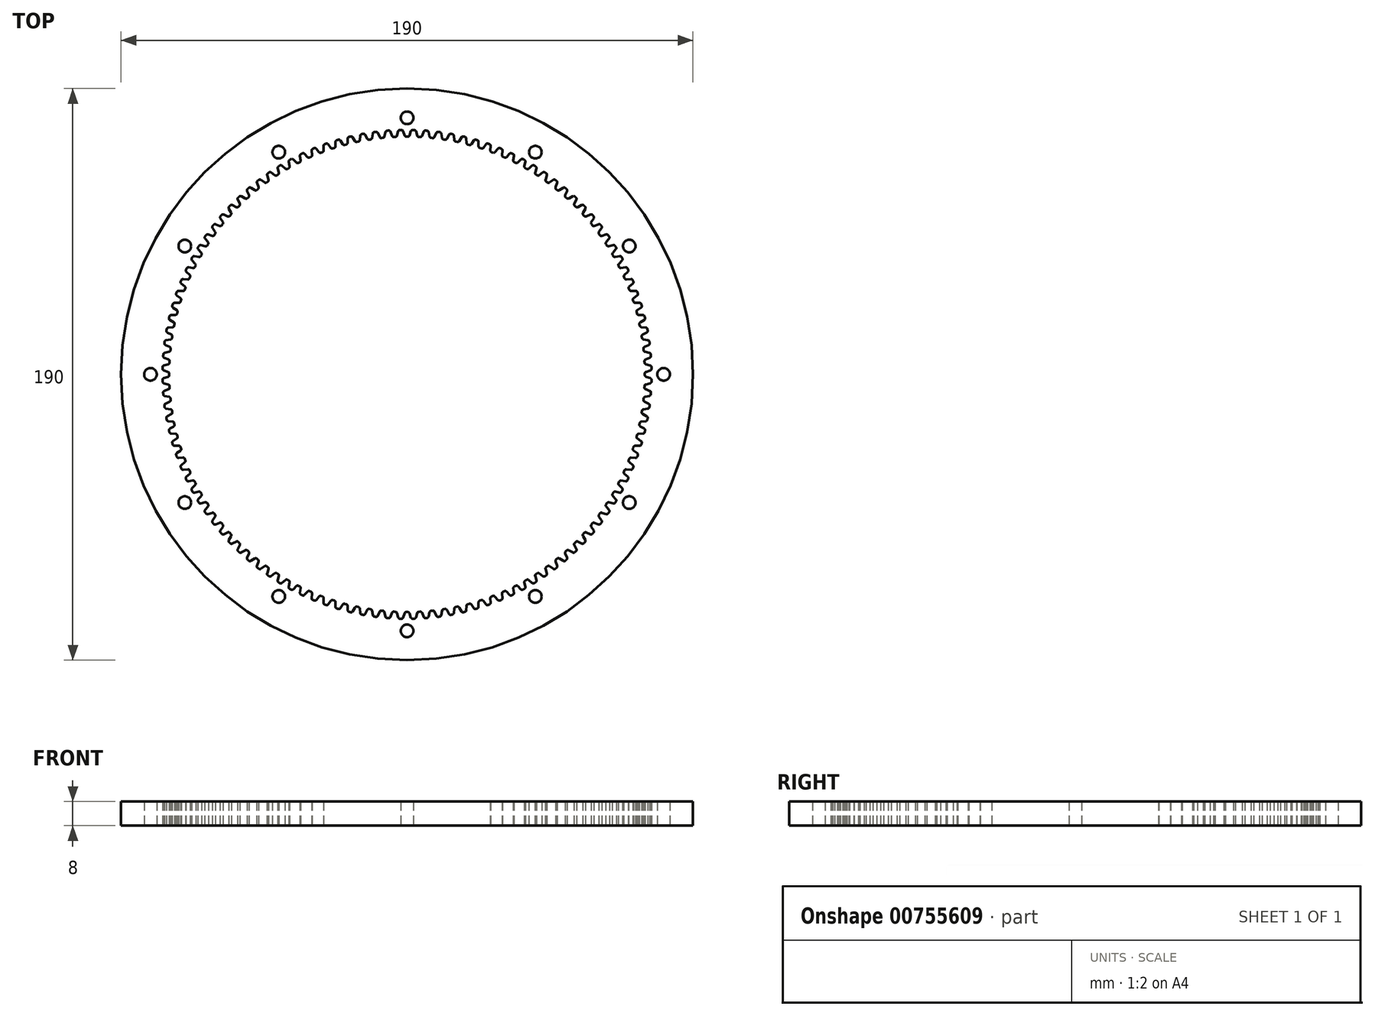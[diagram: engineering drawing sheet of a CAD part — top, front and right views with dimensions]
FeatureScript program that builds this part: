
annotation { "Feature Type Name" : "Feature", "Feature Type Description" : "" }
export const myFeature = defineFeature(function(context is Context, id is Id, definition is map)
    precondition{}
    {
        {
            var Q0;
            Q0=qCreatedBy(makeId("Front.planeOp"),FACE);
            var sketch = newSketch(context, id + "F0", { "sketchPlane" : qUnion([Q0])});
            skLineSegment(sketch, "E0", {"start": v(0, -5) * mm, "end": v(0, 5) * mm, "construction": true});
            skSolve(sketch);
        }
        {
            var Q0;
            Q0=qCreatedBy(makeId("Top.planeOp"),FACE);
            var sketch = newSketch(context, id + "F1", { "sketchPlane" : qUnion([Q0])});
            skLineSegment(sketch, "E1", {"start": v(0, 0) * mm, "end": v(0, 95) * mm, "construction": true});
            skLineSegment(sketch, "E2", {"start": v(0, 0) * mm, "end": v(1.66, 94.99) * mm, "construction": true});
            skLineSegment(sketch, "E3", {"start": v(0, 0) * mm, "end": v(2.49, 94.97) * mm, "construction": true});
            skArc(sketch, "E4", {"start": v(0, 95) * mm, "mid": v(1.24, 95) * mm, "end": v(2.49, 94.97) * mm});
            skLineSegment(sketch, "E5", {"start": v(0, 95) * mm, "end": v(0, 79) * mm});
            skArc(sketch, "E6", {"start": v(1.42, 81.24) * mm, "mid": v(1.77, 81.23) * mm, "end": v(2.13, 81.22) * mm});
            skLineSegment(sketch, "E7", {"start": v(2.13, 81.22) * mm, "end": v(2.49, 94.97) * mm});
            skLineSegment(sketch, "E8", {"start": v(1.42, 81.24) * mm, "end": v(0.69, 79) * mm});
            skLineSegment(sketch, "E9", {"start": v(0.69, 79) * mm, "end": v(0, 79) * mm});
            skArc(sketch, "E10", {"start": v(1.42, 81.24) * mm, "mid": v(0.7, 81.25) * mm, "end": v(0, 81.25) * mm, "construction": true});
            skLineSegment(sketch, "E11", {"start": v(0, 0) * mm, "end": v(0.83, 95) * mm, "construction": true});
            skSolve(sketch);
        }
        {
            var Q0;
            Q0 = qSketchRegion(id + "F1", true);
            extrude(context, id + "F2", {"entities" : qUnion([Q0]), "depth" : 8 * mm, "offsetDistance" : 25 * mm});
        }
        {
            var Q0;
            Q0=makeQuery(id+"F2.opExtrude","SWEPT_EDGE",EDGE,{"disambiguationData":[OSD([sQuery(id+"F1.wireOp",EDGE,"E8"),sQuery(id+"F1.wireOp",EDGE,"E9")])]});
            var Q1;
            Q1=makeQuery(id+"F2.opExtrude","SWEPT_EDGE",EDGE,{"disambiguationData":[OSD([sQuery(id+"F1.wireOp",EDGE,"E6"),sQuery(id+"F1.wireOp",EDGE,"E8")])]});
            fillet(context, id + "F3", {"entities" : qUnion([Q0, Q1]), "radius" : 0.6 * mm, "tangentPropagation" : true, "allowEdgeOverflow" : false});
        }
        {
            var Q0;
            Q0=makeQuery(id+"F2.opExtrude","SWEPT_BODY",BODY,{"disambiguationData":[OSD([sQuery(id+"F1.wireOp",EDGE,"E4"),sQuery(id+"F1.wireOp",EDGE,"E5"),sQuery(id+"F1.wireOp",EDGE,"E6"),sQuery(id+"F1.wireOp",EDGE,"E7"),sQuery(id+"F1.wireOp",EDGE,"E8"),sQuery(id+"F1.wireOp",EDGE,"E9")])]});
            var Q1;
            Q1=makeQuery(id+"F2.opExtrude","SWEPT_FACE",FACE,{"disambiguationData":[OSD([sQuery(id+"F1.wireOp",EDGE,"E5")])]});
            mirror(context, id + "F4", {"operationType" : NewBodyOperationType.ADD, "entities" : qUnion([Q0]), "mirrorPlane" : qUnion([Q1])});
        }
        {
            var Q0;
            Q0=makeQuery(id+"F2.opExtrude","SWEPT_BODY",BODY,{"disambiguationData":[OSD([sQuery(id+"F1.wireOp",EDGE,"E4"),sQuery(id+"F1.wireOp",EDGE,"E5"),sQuery(id+"F1.wireOp",EDGE,"E6"),sQuery(id+"F1.wireOp",EDGE,"E7"),sQuery(id+"F1.wireOp",EDGE,"E8"),sQuery(id+"F1.wireOp",EDGE,"E9")])]});
            var Q1;
            Q1=sQuery(id+"F0.wireOp",EDGE,"E0");
            circularPattern(context, id + "F5", {"operationType" : NewBodyOperationType.ADD, "entities" : qUnion([Q0]), "axis" : qUnion([Q1]), "angle" : 360 * degree, "instanceCount" : 120, "equalSpace" : true});
        }
        {
            var Q0;
            Q0=qCreatedBy(makeId("Top.planeOp"),FACE);
            var sketch = newSketch(context, id + "F6", { "sketchPlane" : qUnion([Q0])});
            skLineSegment(sketch, "E12", {"start": v(0, 0) * mm, "end": v(0, 85.25) * mm});
            skCircle(sketch, "E13", {"center": v(0, 85.25) * mm, "radius": 2.1 * mm});
            skCircle(sketch, "E14.1.0", {"center": v(-42.62, 73.83) * mm, "radius": 2.1 * mm});
            skCircle(sketch, "E14.2.0", {"center": v(-73.83, 42.63) * mm, "radius": 2.1 * mm});
            skCircle(sketch, "E14.3.0", {"center": v(-85.25, 0) * mm, "radius": 2.1 * mm});
            skCircle(sketch, "E14.4.0", {"center": v(-73.83, -42.62) * mm, "radius": 2.1 * mm});
            skCircle(sketch, "E14.5.0", {"center": v(-42.63, -73.83) * mm, "radius": 2.1 * mm});
            skCircle(sketch, "E14.6.0", {"center": v(0, -85.25) * mm, "radius": 2.1 * mm});
            skCircle(sketch, "E14.7.0", {"center": v(42.62, -73.83) * mm, "radius": 2.1 * mm});
            skCircle(sketch, "E14.8.0", {"center": v(73.83, -42.63) * mm, "radius": 2.1 * mm});
            skCircle(sketch, "E14.9.0", {"center": v(85.25, 0) * mm, "radius": 2.1 * mm});
            skCircle(sketch, "E14.10.0", {"center": v(73.83, 42.62) * mm, "radius": 2.1 * mm});
            skCircle(sketch, "E14.11.0", {"center": v(42.62, 73.83) * mm, "radius": 2.1 * mm});
            skPoint(sketch, "E14.center", {"position": v(0, 0) * mm});
            skCircle(sketch, "E15", {"center": v(0, 0) * mm, "radius": 81.25 * mm, "construction": true});
            skSolve(sketch);
        }
        {
            var Q0;
            Q0 = qSketchRegion(id + "F6", true);
            extrude(context, id + "F7", {"entities" : qUnion([Q0]), "operationType" : NewBodyOperationType.REMOVE, "endBound" : BoundingType.THROUGH_ALL, "depth" : 25 * mm, "offsetDistance" : 25 * mm});
        }
    });
